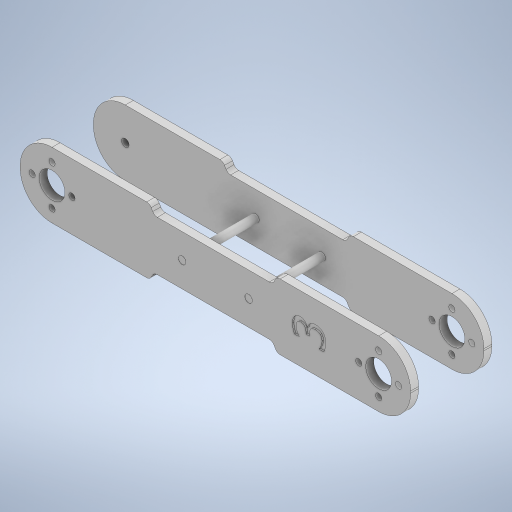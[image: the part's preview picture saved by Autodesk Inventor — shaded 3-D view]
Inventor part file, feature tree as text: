
AUTODESK INVENTOR PART (.ipt)
format: ipt  version: 2023 (Build 270158000, 158)  size: 422,912 bytes
history: native  units: mm
features: extrude x7, sketch x7, other x1, plane x1, mirror x1
ambient origin geometry x8: Origin, YZ Plane, XZ Plane, XY Plane, X Axis, Y Axis, Z Axis, Center Point
bodies: Body1 (feature_tree)
feature tree (17):
  other  "Sólido1"
  extrude  "Extrusión1"  Depth=24.7mm
  extrude  "Extrusión2"  Depth=3.0mm
  extrude  "Extrusión3"  TaperAngle=120.0deg  [1 undecoded]
  plane  "Plano de trabajo1"
  mirror  "Simetría1"
  extrude  "Extrusión4"  Depth=12.0mm
  extrude  "Extrusión5"  Depth=2.0mm
  extrude  "Extrusión6"  Depth=15.0mm
  extrude  "Extrusión7"  Depth=2.3mm
  sketch  "Boceto1"  dims[d0=147.0mm d1=24.7mm]
  sketch  "Boceto2"  dims[d2=12.0mm d5=3.0mm]
  sketch  "Boceto3"  dims[d6=120.0deg d7=120.0deg]
  sketch  "Boceto4"  dims[d8=52.0mm d9=12.0mm]
  sketch  "Boceto5"  dims[d10=2.0mm d11=2.0mm]
  sketch  "Boceto6"  dims[d12=3.0mm d13=0.0mm d14=15.0mm]
  sketch  "Boceto7"  dims[d15=9.7mm d16=2.3mm d17=40.0mm d19=360.0deg d21=3.0mm d22=0.0mm d24=2.8mm d25=2.8mm d26=25.0mm d27=12.5mm d28=10.0mm d29=0.0mm d30=12.3mm d31=10.0mm d32=0.0mm d33=2.8mm d34=10.0mm d35=0.0mm d36=30.5mm d37=0.0mm d38=0.5mm d39=0.0mm]
note: 1 required parameter value undecoded (feature->parameter linkage not recoverable at this tier; creation-order binding heuristic only, values carry confidence <= 0.55)
